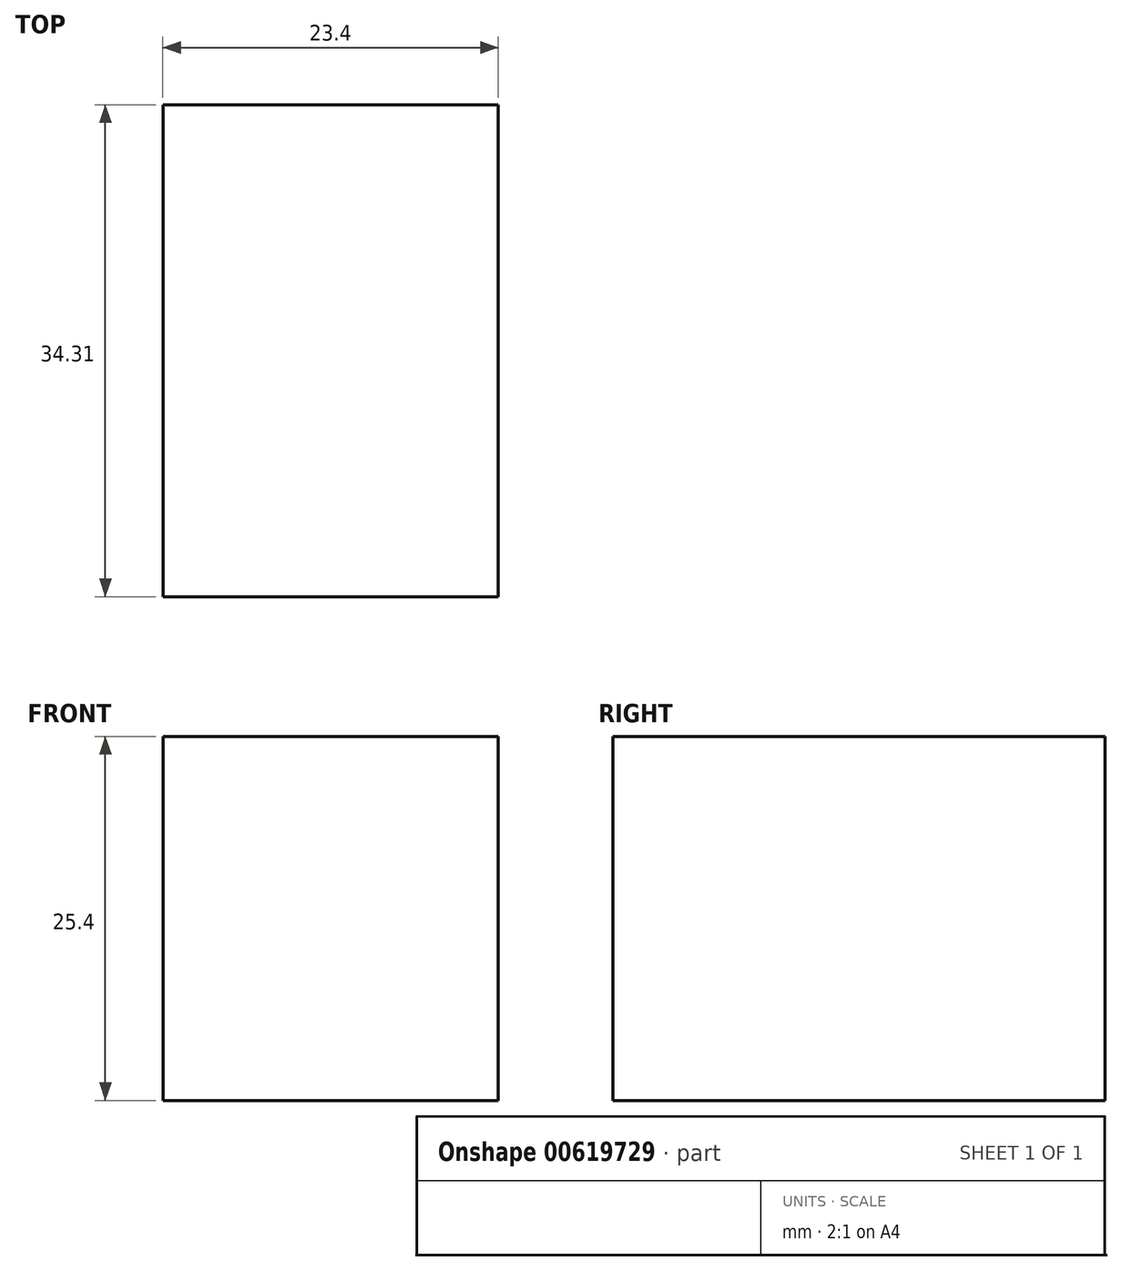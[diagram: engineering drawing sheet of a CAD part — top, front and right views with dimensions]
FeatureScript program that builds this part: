
annotation { "Feature Type Name" : "Feature", "Feature Type Description" : "" }
export const myFeature = defineFeature(function(context is Context, id is Id, definition is map)
    precondition{}
    {
        {
            var Q0;
            Q0=qCreatedBy(makeId("Top.planeOp"),FACE);
            var sketch = newSketch(context, id + "F0", { "sketchPlane" : qUnion([Q0])});
            skLineSegment(sketch, "E0.bottom", {"start": v(29.05, 0) * mm, "end": v(5.65, 0) * mm});
            skLineSegment(sketch, "E0.top", {"start": v(29.05, -34.31) * mm, "end": v(5.65, -34.31) * mm});
            skLineSegment(sketch, "E0.left", {"start": v(29.05, 0) * mm, "end": v(29.05, -34.31) * mm});
            skLineSegment(sketch, "E0.right", {"start": v(5.65, 0) * mm, "end": v(5.65, -34.31) * mm});
            skLineSegment(sketch, "E1.bottom", {"start": v(29.05, -17.16) * mm, "end": v(29.05, -17.16) * mm});
            skLineSegment(sketch, "E1.top", {"start": v(29.05, -12.64) * mm, "end": v(29.05, -12.64) * mm});
            skLineSegment(sketch, "E1.left", {"start": v(29.05, -17.16) * mm, "end": v(29.05, -12.64) * mm});
            skLineSegment(sketch, "E1.right", {"start": v(29.05, -17.16) * mm, "end": v(29.05, -12.64) * mm});
            skSolve(sketch);
        }
        {
            var Q0;
            Q0 = qSketchRegion(id + "F0", true);
            extrude(context, id + "F1", {"entities" : qUnion([Q0]), "depth" : 25.4 * mm, "offsetDistance" : 25.4 * mm});
        }
    });
